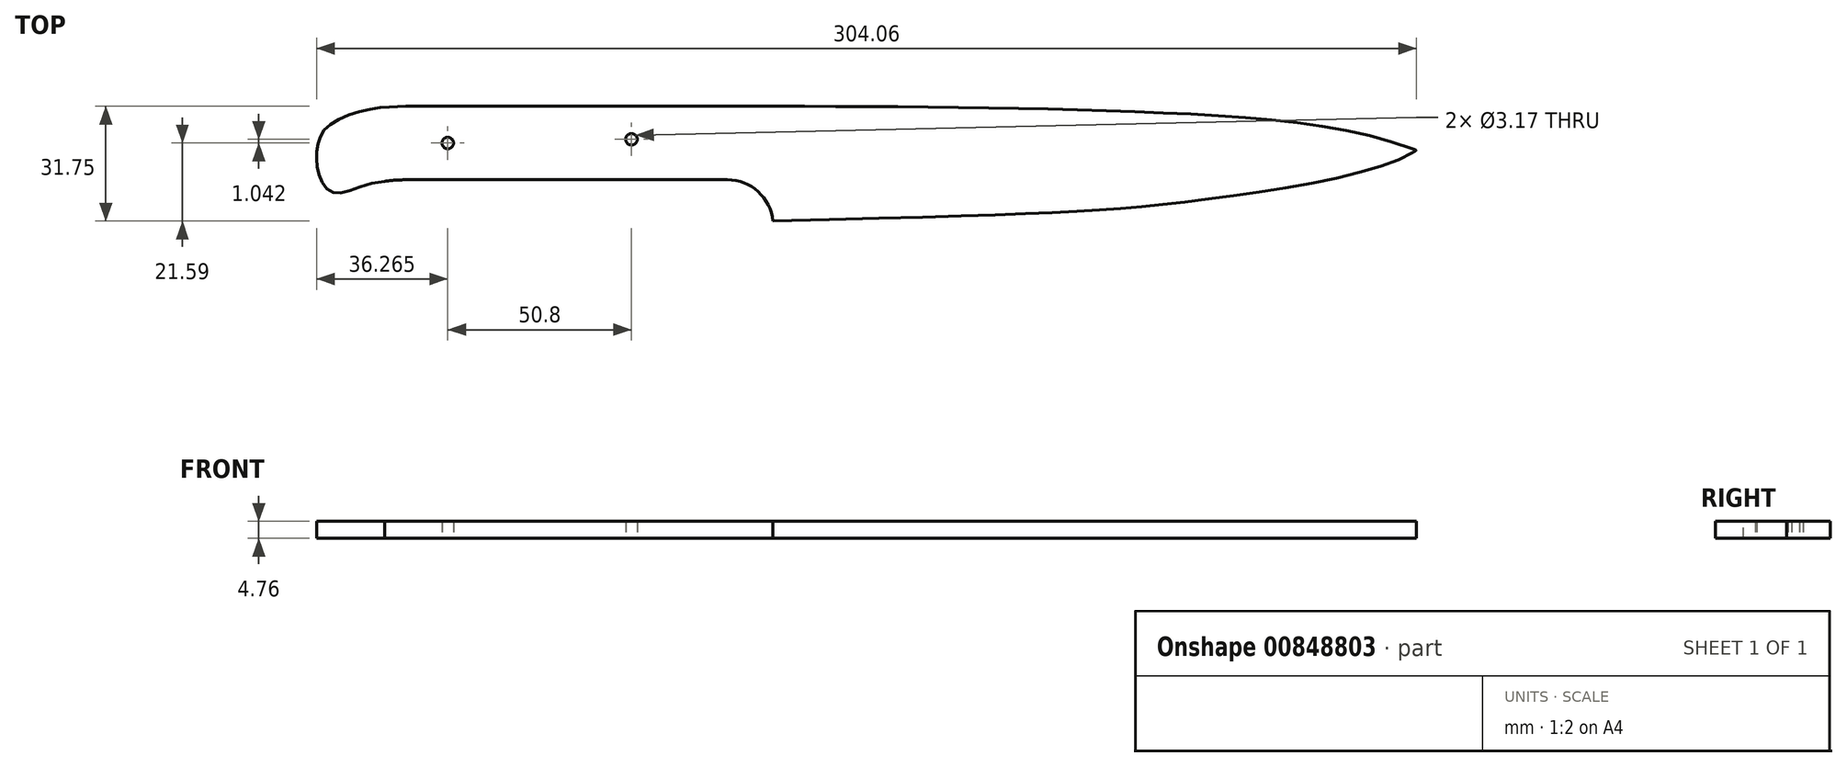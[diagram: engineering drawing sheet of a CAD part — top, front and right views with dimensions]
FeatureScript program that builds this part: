
annotation { "Feature Type Name" : "Feature", "Feature Type Description" : "" }
export const myFeature = defineFeature(function(context is Context, id is Id, definition is map)
    precondition{}
    {
        {
            var Q0;
            Q0=qCreatedBy(makeId("Top.planeOp"),FACE);
            var sketch = newSketch(context, id + "F0", { "sketchPlane" : qUnion([Q0])});
            skLineSegment(sketch, "E0.top", {"start": v(-25.4, 19.05) * mm, "end": v(-127, 19.05) * mm});
            skPoint(sketch, "E0.middle", {"position": v(0, 0) * mm});
            skLineSegment(sketch, "E1", {"start": v(-127, -1.27) * mm, "end": v(-38.1, -1.27) * mm});
            skFitSpline(sketch, "E2", {"points": [v(-25.46, -12.7) * mm, v(91.24, -7.04) * mm, v(152.4, 6.9) * mm], "startDerivative": vector(385.46, 10.55) * mm, "endDerivative": vector(71.6, 49.01) * mm});
            skFitSpline(sketch, "E3", {"points": [v(-25.4, 19.05) * mm, v(79.18, 17.39) * mm, v(152.4, 6.9) * mm], "startDerivative": vector(201.4, 0) * mm, "endDerivative": vector(130.84, -50.08) * mm});
            skFitSpline(sketch, "E4", {"points": [v(-132.86, -1.7) * mm, v(-146.54, -4.96) * mm, v(-150.94, 0) * mm, v(-151.5, 7.21) * mm, v(-148.67, 13.44) * mm, v(-136.51, 18.3) * mm, v(-127, 19.05) * mm], "startDerivative": vector(-86.02, -3.06) * mm, "endDerivative": vector(50.23, 0.35) * mm});
            skArc(sketch, "E5.filletArc", {"start": v(-25.46, -12.7) * mm, "mid": v(-29.58, -4.55) * mm, "end": v(-38.1, -1.27) * mm});
            skArc(sketch, "E6.trimOffspring", {"start": v(-127, -1.27) * mm, "mid": v(-129.94, -1.38) * mm, "end": v(-132.86, -1.7) * mm});
            skPoint(sketch, "E7.orphan", {"position": v(152.4, 19.05) * mm});
            skCircle(sketch, "E8", {"center": v(-115.4, 8.89) * mm, "radius": 1.59 * mm});
            skCircle(sketch, "E9", {"center": v(-64.6, 9.93) * mm, "radius": 1.59 * mm});
            skLineSegment(sketch, "E10", {"start": v(151.4, 7.28) * mm, "end": v(151.4, 6.27) * mm});
            skSolve(sketch);
        }
        {
            var Q0;
            Q0 = qSketchRegion(id + "F0", true);
            extrude(context, id + "F1", {"entities" : qUnion([Q0]), "depth" : 4.76 * mm, "offsetDistance" : 25.4 * mm});
        }
    });
